# Revit family: BL-SH-6012-31BC
name_source: partatom
category: Furniture
units: mm (PartAtom-declared; Revit-internal decimal feet)

## family parameters
Always vertical = Yes
Cut with Voids When Loaded = No
OmniClass Number = 23.40.20.00
OmniClass Title = General Furniture and Specialties
Room Calculation Point = No
Shared = No
Work Plane-Based = No

## types (48) — shared parameters
D = 20"
Default Elevation = 0"
HA 60 = No
zero-valued in all types: ES Book Volume Ct, MS-HS Book Volume Ct

## per-type parameters (varying)
| type | Adder | End | HA 30 | HA 36 | HA 42 | HA 48 | HA 72 | HA 82 | Height | Island | Model | NUMBER PB | Picture book | Starter | Width |
| BL-SH-6012-31PB-A-FB-HA30 | No | No | Yes | No | No | No | No | No | 30" | No | BL-SH-6012-31PB-A-FB-FB-HA30 | 2 | Yes | No | 36" |
| BL-SH-6012-31PB-A-FB-HA42 | No | No | No | No | Yes | No | No | No | 42" | No | BL-SH-6012-31PB-A-FB-FB-HA42 | 2 | Yes | No | 36" |
| BL-SH-6012-31PB-A-FB-HA48 | No | No | No | No | No | Yes | No | No | 42" | No | BL-SH-6012-31PB-A-FB-FB-HA48 | 2 | Yes | No | 36" |
| BL-SH-6012-31PB-A-FB-HA72 | No | No | No | No | No | No | Yes | No | 42" | No | BL-SH-6012-31PB-A-FB-FB-HA72 | 2 | Yes | No | 36" |
| BL-SH-6012-31PB-A-FB-HA82 | No | No | No | No | No | No | No | Yes | 42" | No | BL-SH-6012-31PB-A-FB-FB-HA82 | 2 | Yes | No | 36" |
| BL-SH-6012-31PB-E-FB | No | Yes | No | No | No | No | No | No | 42" | No | BL-SH-6012-31PB-E-FB-FB | 2 | Yes | No | 36" |
| BL-SH-6012-31PB-I-FB | No | No | No | No | No | No | No | No | 42" | Yes | BL-SH-6012-31PB-I-FB-FB | 2 | Yes | No | 36" |
| BL-SH-6012-31PB-S-FB | Yes | No | No | No | No | No | No | No | 42" | No | BL-SH-6012-31PB-S-FB-FB | 2 | Yes | Yes | 36" |
| BL-SH-6012-31PB-S-FB-HA42 | No | No | No | No | Yes | No | No | No | 42" | No | BL-SH-6012-31PB-S-FB-FB-HA42 | 2 | Yes | Yes | 36" |
| BL-SH-6012-31PB-S-FB-HA48 | No | No | No | No | No | Yes | No | No | 42" | No | BL-SH-6012-31PB-S-FB-FB-HA48 | 2 | Yes | Yes | 36" |
| BL-SH-6012-31PB-S-FB-HA72 | No | No | No | No | No | No | Yes | No | 42" | No | BL-SH-6012-31PB-S-FB-FB-HA72 | 2 | Yes | Yes | 36" |
| BL-SH-6012-31PB-S-FB-HA82 | No | No | No | No | No | No | No | Yes | 42" | No | BL-SH-6012-31PB-S-FB-FB-HA82 | 2 | Yes | Yes | 36" |
| BL-SH-6012-31BC-S-FB-HA30 | No | No | Yes | No | No | No | No | No | 42" | No | BL-SH-6012-31BC-S-FB-FB-HA30 | 2 | No | Yes | 36" |
| BL-SH-6012-31PB-S-FB-HA30 | No | No | Yes | No | No | No | No | No | 42" | No | BL-SH-6012-31PB-S-FB-FB-HA30 | 2 | Yes | Yes | 36" |
| BL-SH-6012-31MS-A-FB | Yes | No | No | No | No | No | No | No | 42" | No | BL-SH-6012-31MS-A-FB-FB | 2 | No | No | 36" |
| BL-SH-6012-31MS-A-FB-HA30 | No | No | Yes | No | No | No | No | No | 42" | No | BL-SH-6012-31MS-A-FB-FB-HA30 | 2 | No | No | 36" |
| BL-SH-6012-31MS-A-FB-HA42 | No | No | No | No | Yes | No | No | No | 42" | No | BL-SH-6012-31MS-A-FB-FB-HA42 | 2 | No | No | 36" |
| BL-SH-6012-31MS-A-FB-HA48 | No | No | No | No | No | Yes | No | No | 42" | No | BL-SH-6012-31MS-A-FB-FB-HA48 | 2 | No | No | 36" |
| BL-SH-6012-31MS-A-FB-HA72 | No | No | No | No | No | No | Yes | No | 42" | No | BL-SH-6012-31MS-A-FB-FB-HA72 | 2 | No | No | 36" |
| BL-SH-6012-31MS-A-FB-HA82 | No | No | No | No | No | No | No | Yes | 42" | No | BL-SH-6012-31MS-A-FB-FB-HA82 | 2 | No | No | 36" |
| BL-SH-6012-31MS-E-FB | No | Yes | No | No | No | No | No | No | 42" | No | BL-SH-6012-31MS-E-FB-FB | 2 | No | No | 36" |
| BL-SH-6012-31MS-I-FB | No | No | No | No | No | No | No | No | 42" | Yes | BL-SH-6012-31MS-I-FB-FB | 2 | No | No | 36" |
| BL-SH-6012-31MS-S-FB | Yes | No | No | No | No | No | No | No | 42" | No | BL-SH-6012-31MS-S-FB-FB | 2 | No | Yes | 36" |
| BL-SH-6012-31MS-S-FB-HA30 | No | No | Yes | No | No | No | No | No | 42" | No | BL-SH-6012-31MS-S-FB-FB-HA30 | 2 | No | Yes | 36" |
| BL-SH-6012-31MS-S-FB-HA42 | No | No | No | No | Yes | No | No | No | 42" | No | BL-SH-6012-31MS-S-FB-FB-HA42 | 2 | No | Yes | 36" |
| BL-SH-6012-31MS-S-FB-HA48 | No | No | No | No | No | Yes | No | No | 42" | No | BL-SH-6012-31MS-S-FB-FB-HA48 | 2 | No | Yes | 36" |
| BL-SH-6012-31MS-S-FB-HA72 | No | No | No | No | No | No | Yes | No | 42" | No | BL-SH-6012-31MS-S-FB-FB-HA72 | 2 | No | Yes | 36" |
| BL-SH-6012-31MS-S-FB-HA82 | No | No | No | No | No | No | No | Yes | 42" | No | BL-SH-6012-31MS-S-FB-FB-HA82 | 5 | No | Yes | 48" |
| BL-SH-6012-31PB-A-FB | Yes | No | No | No | No | No | No | No | 42" | No | BL-SH-6012-31PB-A-FB-FB | 2 | Yes | No | 36" |
| BL-SH-6012-31BC-A-FB-HA30 | No | No | Yes | No | No | No | No | No | 42" | No | BL-SH-6012-31BC-A-FB-FB-HA30 | 2 | No | No | 36" |
| BL-SH-6012-31BC-A-FB-HA82 | No | No | No | No | No | No | No | Yes | 42" | No | BL-SH-6012-31BC-A-FB-FB-HA82 | 2 | No | No | 36" |
| BL-SH-6012-31BC-A-FB-HA48 | No | No | No | No | No | Yes | No | No | 42" | No | BL-SH-6012-31BC-A-FB-FB-HA48 | 2 | No | No | 36" |
| BL-SH-6012-31BC-A-FB-HA42 | No | No | No | No | Yes | No | No | No | 42" | No | BL-SH-6012-31BC-A-FB-FB-HA42 | 2 | No | No | 36" |
| BL-SH-6012-31BC-A-FB-HA72 | No | No | No | No | No | No | Yes | No | 42" | No | BL-SH-6012-31BC-A-FB-FB-HA72 | 2 | No | No | 36" |
| BL-SH-6012-31BC-S-FB-HA42 | No | No | No | No | Yes | No | No | No | 42" | No | BL-SH-6012-31BC-S-FB-FB-HA42 | 2 | No | Yes | 36" |
| BL-SH-6012-31BC-S-FB-HA48 | No | No | No | No | No | Yes | No | No | 42" | No | BL-SH-6012-31BC-S-FB-FB-HA48 | 2 | No | Yes | 36" |
| BL-SH-6012-31BC-S-FB-HA72 | No | No | No | No | No | No | Yes | No | 42" | No | BL-SH-6012-31BC-S-FB-FB-HA72 | 2 | No | Yes | 36" |
| BL-SH-6012-31BC-S-FB-HA82 | No | No | No | No | No | No | No | Yes | 42" | No | BL-SH-6012-31BC-S-FB-FB-HA82 | 2 | No | Yes | 36" |
| BL-SH-6012-31BC-I-FB | No | No | No | No | No | No | No | No | 42" | Yes | BL-SH-6012-31BC-I-FB-FB | 2 | No | No | 36" |
| BL-SH-6012-31BC-S-FB | Yes | No | No | No | No | No | No | No | 42" | No | BL-SH-6012-31BC-S-FB-FB | 2 | No | Yes | 36" |
| BL-SH-6012-31BC-A-FB | Yes | No | No | No | No | No | No | No | 42" | No | BL-SH-6012-31BC-A-FB-FB | 2 | No | No | 36" |
| BL-SH-6012-31BC-E-FB | No | Yes | No | No | No | No | No | No | 42" | No | BL-SH-6012-31MS-S-FB-FB-HA82 | 2 | No | No | 36" |
| BL-SH-6012-31BC-A-FB-HA36 | No | No | No | Yes | No | No | No | No | 42" | No | BL-SH-6012-31BC-A-FB-FB-HA36 | 2 | No | No | 36" |
| BL-SH-6012-31PB-A-FB-HA36 | No | No | No | Yes | No | No | No | No | 42" | No | BL-SH-6012-31BC-A-FB-FB-HA36 | 2 | Yes | No | 36" |
| BL-SH-6012-31MS-S-FB-HA36 | No | No | No | Yes | No | No | No | No | 42" | No | BL-SH-6012-31MS-S-FB-FB-HA36 | 2 | No | Yes | 36" |
| BL-SH-6012-31MS-A-FB-HA36 | No | No | No | Yes | No | No | No | No | 42" | No | BL-SH-6012-31MS-A-FB-FB-HA36 | 2 | No | No | 36" |
| BL-SH-6012-31PB-S-FB-HA36 | No | No | No | Yes | No | No | No | No | 42" | No | BL-SH-6012-31PB-S-FB-FB-HA36 | 2 | Yes | Yes | 36" |
| BL-SH-6012-31BC-S-FB-HA36 | No | No | No | Yes | No | No | No | No | 42" | No | BL-SH-6012-31BC-S-FB-FB-HA36 | 2 | No | Yes | 36" |

## geometry (parser evidence)
native form markers: Sweep x17
no freeform markers — native parametric forms only
